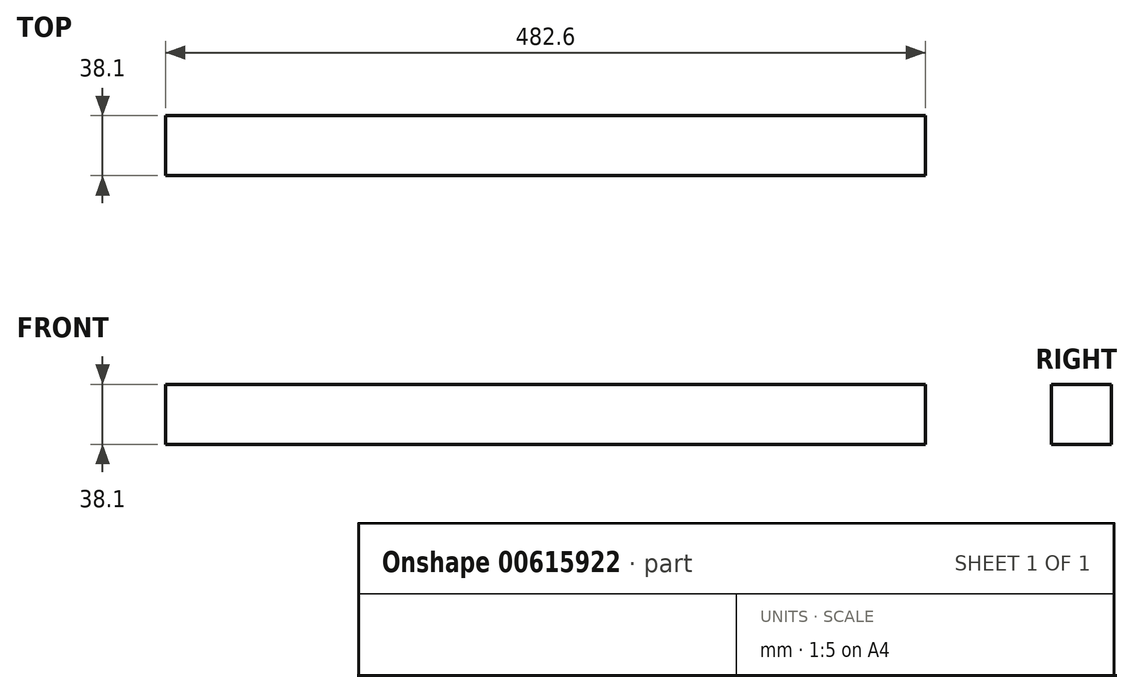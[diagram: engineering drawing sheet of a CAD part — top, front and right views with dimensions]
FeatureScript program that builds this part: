
annotation { "Feature Type Name" : "Feature", "Feature Type Description" : "" }
export const myFeature = defineFeature(function(context is Context, id is Id, definition is map)
    precondition{}
    {
        {
            var Q0;
            Q0=qCreatedBy(makeId("Front.planeOp"),FACE);
            var sketch = newSketch(context, id + "F0", { "sketchPlane" : qUnion([Q0])});
            skLineSegment(sketch, "E0.bottom", {"start": v(-241.3, 19.05) * mm, "end": v(241.3, 19.05) * mm});
            skLineSegment(sketch, "E0.top", {"start": v(-241.3, -19.05) * mm, "end": v(241.3, -19.05) * mm});
            skLineSegment(sketch, "E0.left", {"start": v(-241.3, 19.05) * mm, "end": v(-241.3, -19.05) * mm});
            skLineSegment(sketch, "E0.right", {"start": v(241.3, 19.05) * mm, "end": v(241.3, -19.05) * mm});
            skPoint(sketch, "E0.middle", {"position": v(0, 0) * mm});
            skSolve(sketch);
        }
        {
            var Q0;
            Q0 = qSketchRegion(id + "F0", true);
            extrude(context, id + "F1", {"entities" : qUnion([Q0]), "endBound" : BoundingType.SYMMETRIC, "depth" : 38.1 * mm, "offsetDistance" : 25.4 * mm});
        }
    });
